# Revit family: Profile+Cover_63_UN_Surface-Mounted-Pendant_NAL
name_source: partatom
category: Lighting Fixtures
units: mm (PartAtom-declared; Revit-internal decimal feet)

## family parameters
Always vertical = No
Cut with Voids When Loaded = No
Light Source = No
OmniClass Number = 23.80.70.00
OmniClass Title = Lighting
Part Type = Normal
Room Calculation Point = Yes
Round Connector Dimension = Use Diameter
Shared = No
Work Plane-Based = No

## types (2) — shared parameters
Apparent Load = 0 VA
Assembly Code = 63.0
Description = Surface-mounted or pendant profile
Geometry = Linear Lightline - Profile Geometry : Profile + Cover plate
IfcExportAs = IfcLightFixtureType
IfcExportType = USERDEFINED
Lamp = LED
Luminaire_Body_Material = PPS Plastic
Luminaire_Cap_Material = PPS Plastic
Manufacturer = Natec Lighting B.V.
Model = Linear Lightline
URL = https://nateclighting.nl
Voltage = 230 V
Wattage Comments = 16W

## per-type parameters (varying)
| type | Sensor |
| Cover Plate | No |
| Cover Plate + Sensor | Yes |

## geometry (parser evidence)
native form markers: Extrusion x1, Sweep x19
no freeform markers — native parametric forms only
